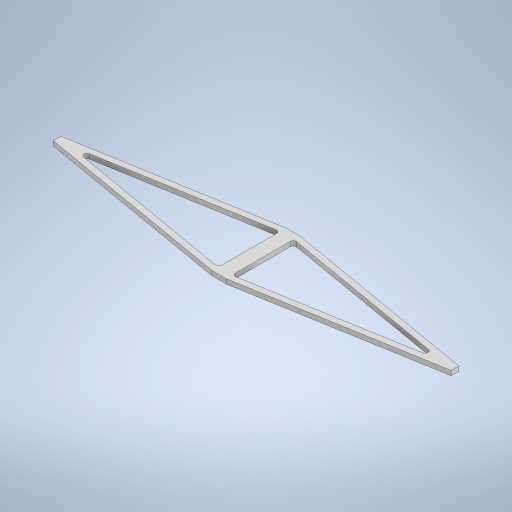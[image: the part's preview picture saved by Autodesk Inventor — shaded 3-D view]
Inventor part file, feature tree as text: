
AUTODESK INVENTOR PART (.ipt)
format: ipt  version: 2023 (Build 270158000, 158)  size: 282,112 bytes
history: native  units: mm
features: extrude x1, fillet x1, sketch x1
ambient origin geometry x8: Origin, YZ Plane, XZ Plane, XY Plane, X Axis, Y Axis, Z Axis, Center Point
bodies: Solid1 (feature_tree)
feature tree (3):
  extrude  "Main_block"  Depth=6.35mm TaperAngle=0.0deg
  fillet  "Fillet7"  Radius=600.0mm
  sketch  "Sketch1"  dims[d6=100.0mm d8=6.35mm d9=0.0mm d36=600.0mm d38=10.0mm d39=100.0mm d42=540.0mm d44=8.0mm d45=8.0mm d46=4.0mm d37=0.0mm d47=0.0mm d48=0.0mm d49=0.0mm]
